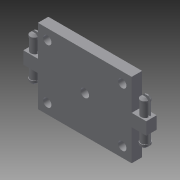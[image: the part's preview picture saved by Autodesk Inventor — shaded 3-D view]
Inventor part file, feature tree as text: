
AUTODESK INVENTOR PART (.ipt)
format: ipt  version: 2015 (Build 190159000, 159)  size: 266,752 bytes
history: native  units: in
note: dims shown in document units (in); Inventor stores cm internally (conversion verified against a paired STEP export)
features: sketch x6, extrude x5, projected_geometry x5, chamfer x2, plane x1, mirror x1
ambient origin geometry x8: Origin, YZ Plane, XZ Plane, XY Plane, X Axis, Y Axis, Z Axis, Center Point
bodies: Solid1 (feature_tree)
feature tree (20):
  extrude  "Extrusion1"  Depth=0.1575in
  extrude  "Extrusion2"  Depth=1.0236in
  extrude  "Extrusion3"  Depth=0.1969in TaperAngle=0.0deg
  extrude  "Extrusion4"  Depth=1.7717in
  extrude  "Extrusion5"  Depth=0.2362in
  sketch  "Sketch7"  dims[d12=0.1575in d13=0.1181in d14=0.0984in d15=0.0197in d16=0.0197in d19=0.0787in d20=0.0787in d21=0.2362in d22=0.4331in d23=0.0in d24=0.0in d27=0.0787in d28=0.0in d29=0.0394in d30=0.0787in d31=45.0deg d32=0.0079in d33=0.0118in d35=0.0118in d36=0.0118in d37=0.0787in d38=0.0787in d39=0.0in d40=0.0394in d41=0.0787in d42=45.0deg]
  plane  "Work Plane1"
  mirror  "Mirror1"
  chamfer  "Chamfer1"  Distance=0.1181in
  chamfer  "Chamfer2"  Distance=0.0984in
  sketch  "Sketch1"  dims[d0=0.1969in d1=0.0in d2=0.1575in]
  sketch  "Sketch2"  dims[d3=1.4173in d4=1.0236in]
  sketch  "Sketch3"  dims[d5=0.1614in d6=0.1969in d7=0.0in]
  sketch  "Sketch4"  dims[d8=1.4134in d9=1.7717in]
  projected_geometry  "Projected Loop1"
  projected_geometry  "Projected Loop2"
  sketch  "Sketch5"  dims[d10=0.2362in d11=2.3228in]
  projected_geometry  "Projected Loop3"
  projected_geometry  "Projected Loop4"
  projected_geometry  "Projected Loop6"
